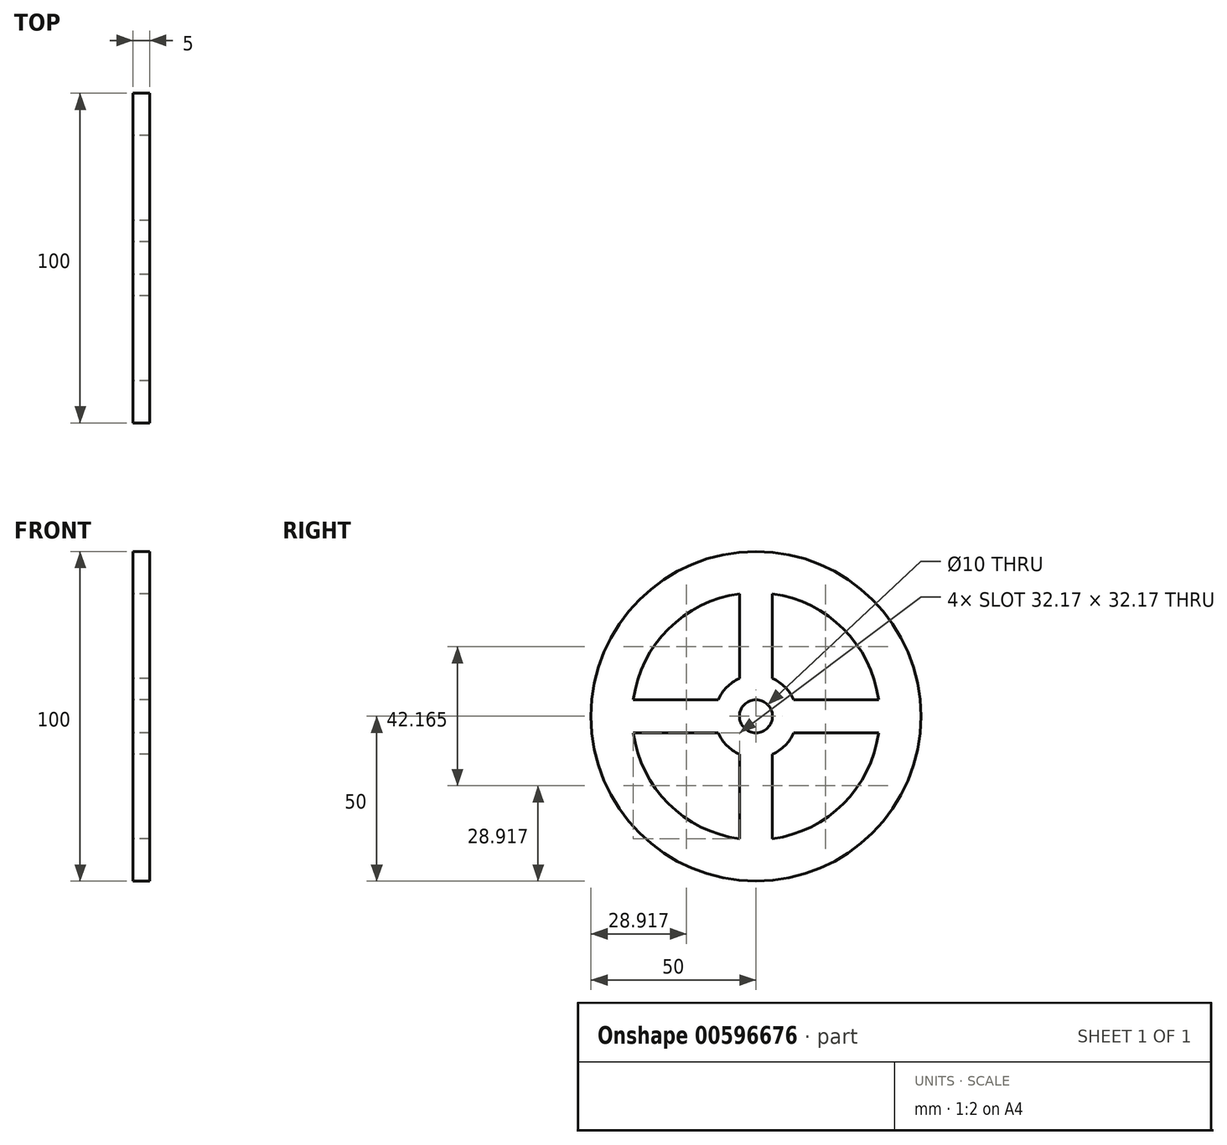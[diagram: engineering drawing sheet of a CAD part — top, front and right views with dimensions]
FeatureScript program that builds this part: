
annotation { "Feature Type Name" : "Feature", "Feature Type Description" : "" }
export const myFeature = defineFeature(function(context is Context, id is Id, definition is map)
    precondition{}
    {
        {
            var Q0;
            Q0=qCreatedBy(makeId("Right.planeOp"),FACE);
            var sketch = newSketch(context, id + "F0", { "sketchPlane" : qUnion([Q0])});
            skCircle(sketch, "E0", {"center": v(0, 0) * mm, "radius": 50 * mm});
            skArc(sketch, "E1", {"start": v(5, -37.17) * mm, "mid": v(26.52, -26.52) * mm, "end": v(37.17, -5) * mm});
            skArc(sketch, "E2", {"start": v(-5, 11.46) * mm, "mid": v(-8.84, 8.84) * mm, "end": v(-11.46, 5) * mm});
            skCircle(sketch, "E3", {"center": v(0, 0) * mm, "radius": 5 * mm});
            skLineSegment(sketch, "E4", {"start": v(0, 65.65) * mm, "end": v(0, -62.9) * mm, "construction": true});
            skLineSegment(sketch, "E5", {"start": v(-56.2, 0) * mm, "end": v(63.53, 0) * mm, "construction": true});
            skLineSegment(sketch, "E6.0", {"start": v(-5, 37.17) * mm, "end": v(-5, 11.46) * mm});
            skLineSegment(sketch, "E7.0", {"start": v(5, 37.17) * mm, "end": v(5, 11.46) * mm});
            skLineSegment(sketch, "E8.0", {"start": v(-37.17, -5) * mm, "end": v(-11.46, -5) * mm});
            skLineSegment(sketch, "E9.0", {"start": v(-37.17, 5) * mm, "end": v(-11.46, 5) * mm});
            skLineSegment(sketch, "E10.trimOffspring", {"start": v(-5, -11.46) * mm, "end": v(-5, -37.17) * mm});
            skLineSegment(sketch, "E11.trimOffspring", {"start": v(5, -11.46) * mm, "end": v(5, -37.17) * mm});
            skLineSegment(sketch, "E12.trimOffspring", {"start": v(11.46, -5) * mm, "end": v(37.17, -5) * mm});
            skLineSegment(sketch, "E13.trimOffspring", {"start": v(11.46, 5) * mm, "end": v(37.17, 5) * mm});
            skArc(sketch, "E14.trimOffspring", {"start": v(-11.46, -5) * mm, "mid": v(-8.84, -8.84) * mm, "end": v(-5, -11.46) * mm});
            skArc(sketch, "E15.trimOffspring", {"start": v(11.46, 5) * mm, "mid": v(8.84, 8.84) * mm, "end": v(5, 11.46) * mm});
            skArc(sketch, "E16.trimOffspring", {"start": v(5, -11.46) * mm, "mid": v(8.84, -8.84) * mm, "end": v(11.46, -5) * mm});
            skArc(sketch, "E17.trimOffspring", {"start": v(37.17, 5) * mm, "mid": v(26.52, 26.52) * mm, "end": v(5, 37.17) * mm});
            skArc(sketch, "E18.trimOffspring", {"start": v(-5, 37.17) * mm, "mid": v(-26.52, 26.52) * mm, "end": v(-37.17, 5) * mm});
            skArc(sketch, "E19.trimOffspring", {"start": v(-37.17, -5) * mm, "mid": v(-26.52, -26.52) * mm, "end": v(-5, -37.17) * mm});
            skSolve(sketch);
        }
        {
            var Q0;
            Q0=makeQuery(id+"F0.imprint","IMPRINT",FACE,{"disambiguationData":[TD([[makeQuery(id+"F0.imprint","IMPRINT",EDGE,{"derivedFrom":sQuery(id+"F0.wireOp",EDGE,"E0")}),1.0]])]});
            extrude(context, id + "F1", {"entities" : qUnion([Q0]), "depth" : 5 * mm, "offsetDistance" : 25 * mm});
        }
    });
